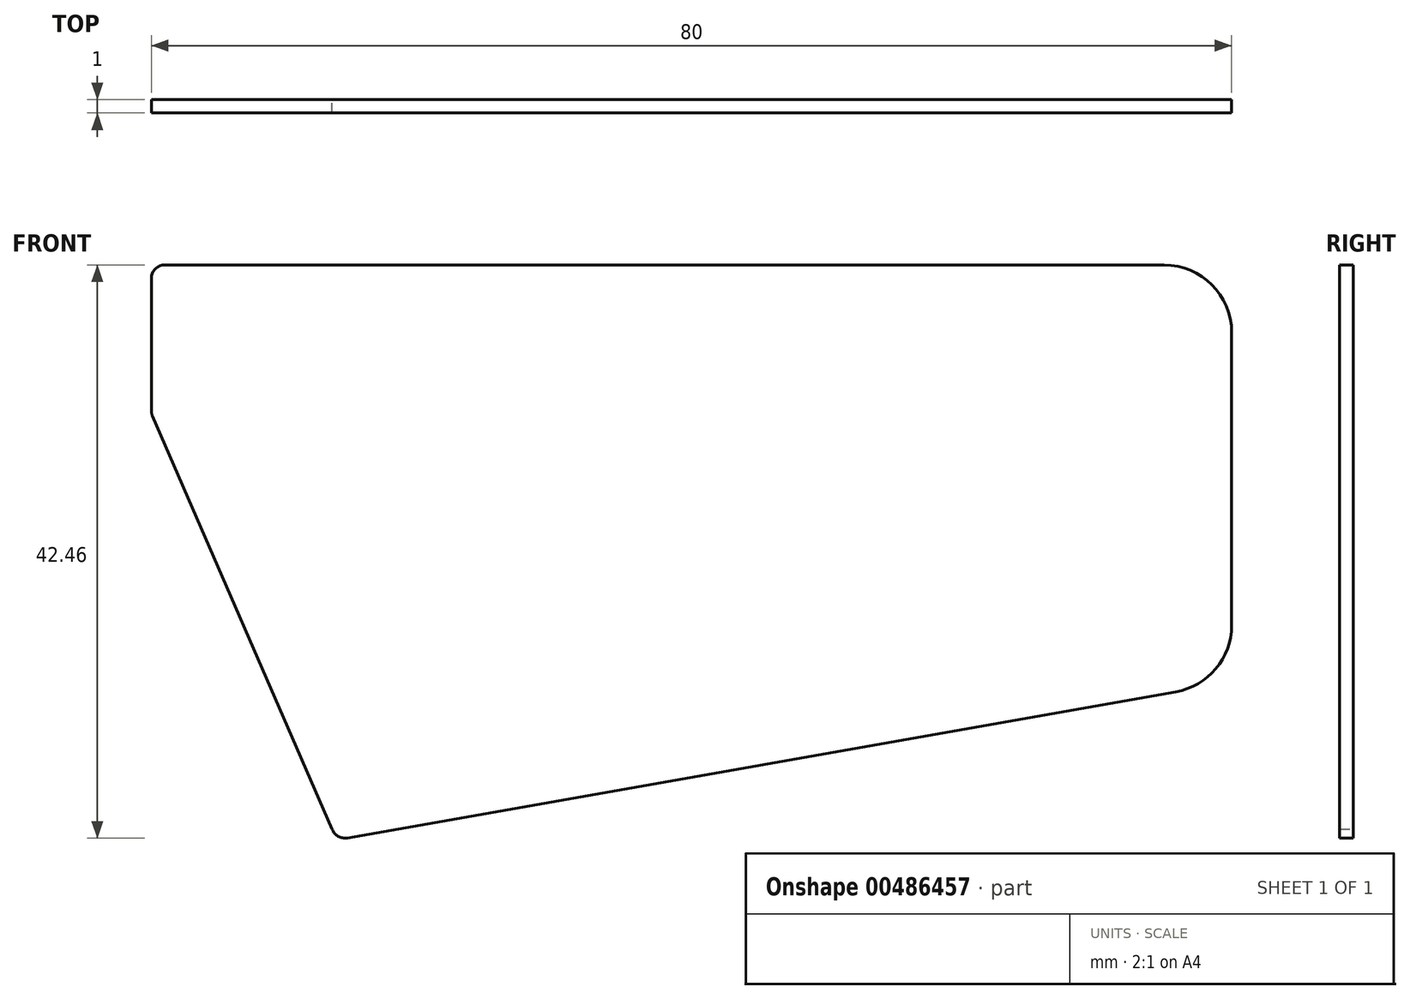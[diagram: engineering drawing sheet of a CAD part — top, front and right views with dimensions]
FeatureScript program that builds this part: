
annotation { "Feature Type Name" : "Feature", "Feature Type Description" : "" }
export const myFeature = defineFeature(function(context is Context, id is Id, definition is map)
    precondition{}
    {
        {
            var Q0;
            Q0=qCreatedBy(makeId("Front.planeOp"),FACE);
            var sketch = newSketch(context, id + "F0", { "sketchPlane" : qUnion([Q0])});
            skLineSegment(sketch, "E0", {"start": v(14.5, -37.44) * mm, "end": v(75.87, -26.62) * mm});
            skLineSegment(sketch, "E1", {"start": v(80, 0) * mm, "end": v(80, -21.7) * mm});
            skPoint(sketch, "E2.visualSharp", {"position": v(0, 0) * mm});
            skPoint(sketch, "E3.visualSharp", {"position": v(13.68, -37.59) * mm});
            skArc(sketch, "E3.filletArc", {"start": v(13.4, -36.8) * mm, "mid": v(13.83, -37.32) * mm, "end": v(14.5, -37.44) * mm});
            skPoint(sketch, "E4.visualSharp", {"position": v(80, -25.9) * mm});
            skArc(sketch, "E4.filletArc", {"start": v(75.87, -26.62) * mm, "mid": v(78.83, -24.91) * mm, "end": v(80, -21.7) * mm});
            skLineSegment(sketch, "E5", {"start": v(1, 5) * mm, "end": v(75, 5) * mm});
            skPoint(sketch, "E6.visualSharp", {"position": v(80, 5) * mm});
            skArc(sketch, "E6.filletArc", {"start": v(80, 0) * mm, "mid": v(78.54, 3.54) * mm, "end": v(75, 5) * mm});
            skPoint(sketch, "E7.visualSharp", {"position": v(0, 5) * mm});
            skArc(sketch, "E7.filletArc", {"start": v(1, 5) * mm, "mid": v(0.3, 4.7) * mm, "end": v(0, 4) * mm});
            skLineSegment(sketch, "E8", {"start": v(0, 4) * mm, "end": v(0, -5.8) * mm});
            skLineSegment(sketch, "E9", {"start": v(0.08, -6.2) * mm, "end": v(13.4, -36.8) * mm});
            skPoint(sketch, "E10.visualSharp", {"position": v(0, -6) * mm});
            skArc(sketch, "E10.filletArc", {"start": v(0, -5.8) * mm, "mid": v(0.02, -6) * mm, "end": v(0.08, -6.2) * mm});
            skSolve(sketch);
        }
        {
            var Q0;
            Q0=makeQuery(id+"F0.imprint","IMPRINT",FACE,{"disambiguationData":[TD([[makeQuery(id+"F0.imprint","IMPRINT",EDGE,{"derivedFrom":sQuery(id+"F0.wireOp",EDGE,"E0")}),1.0]])]});
            extrude(context, id + "F1", {"entities" : qUnion([Q0]), "endBound" : BoundingType.SYMMETRIC, "depth" : 1 * mm, "offsetDistance" : 25 * mm});
        }
    });
